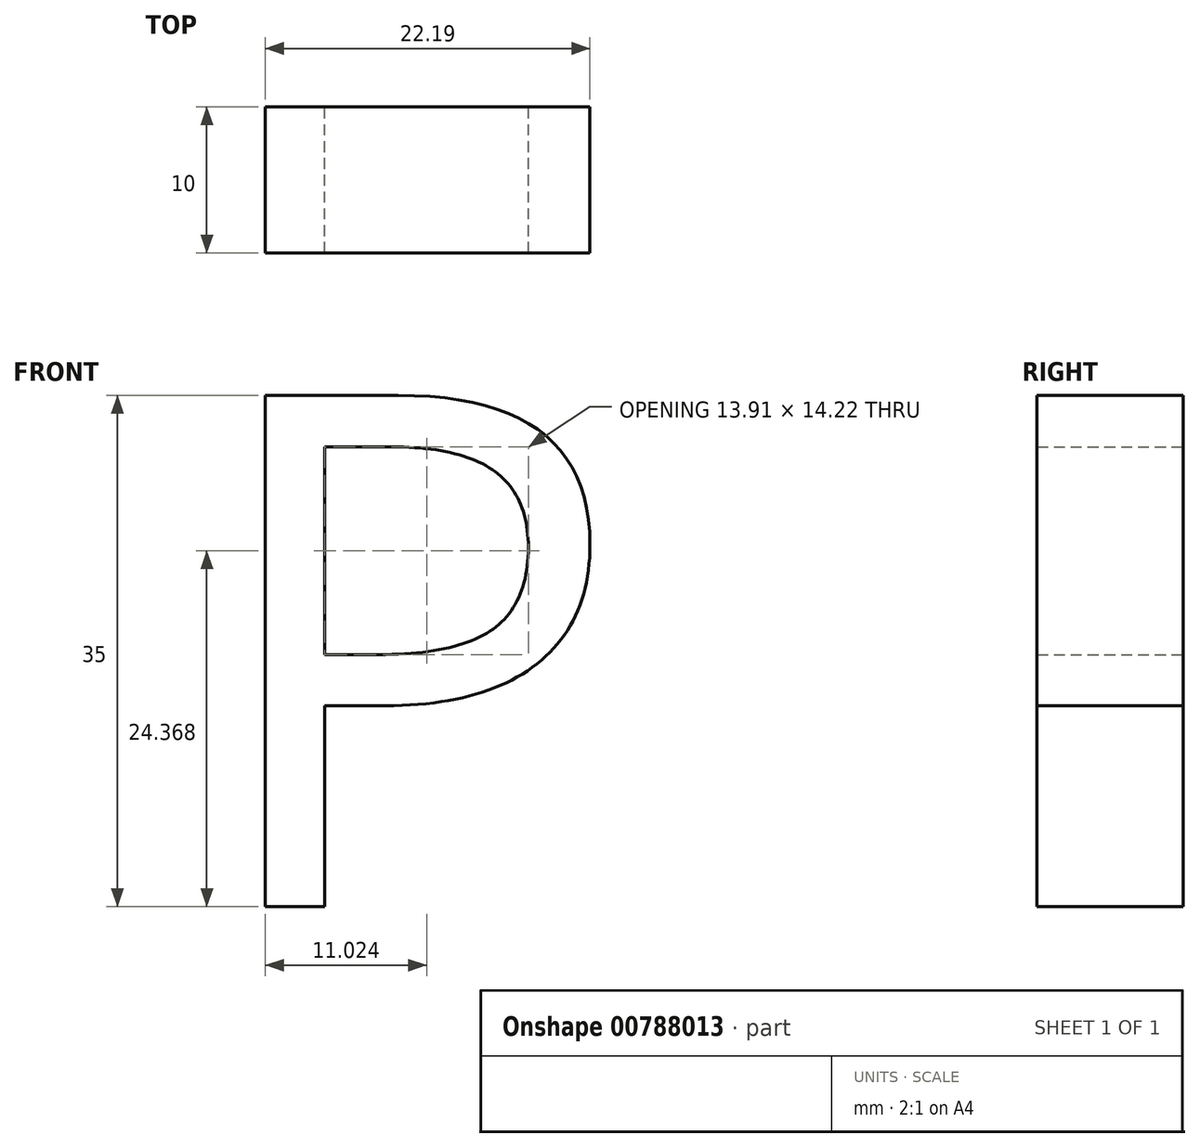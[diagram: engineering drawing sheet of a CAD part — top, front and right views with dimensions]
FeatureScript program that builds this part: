
annotation { "Feature Type Name" : "Feature", "Feature Type Description" : "" }
export const myFeature = defineFeature(function(context is Context, id is Id, definition is map)
    precondition{}
    {
        {
            var Q0;
            Q0=qCreatedBy(makeId("Front.planeOp"),FACE);
            var sketch = newSketch(context, id + "F0", { "sketchPlane" : qUnion([Q0])});
            skText(sketch, "E0", { "text": "P", "fontName": "OpenSans-Regular.ttf"});
            const initialGuessF0  = {"E0": [-0.03019, 0, 1, 0, 0.0353]};
            skSetInitialGuess(sketch, initialGuessF0);
            skSolve(sketch);
        }
        {
            var Q0;
            Q0=makeQuery(id+"F0.imprint","IMPRINT",FACE,{"disambiguationData":[TD([[makeQuery(id+"F0.imprint","IMPRINT",EDGE,{"derivedFrom":sQuery(id+"F0.wireOp",EDGE,"E0.sketch_text.stroke-0")}),-1.0]])]});
            extrude(context, id + "F1", {"entities" : qUnion([Q0]), "depth" : 10 * mm, "offsetDistance" : 25.4 * mm});
        }
    });
